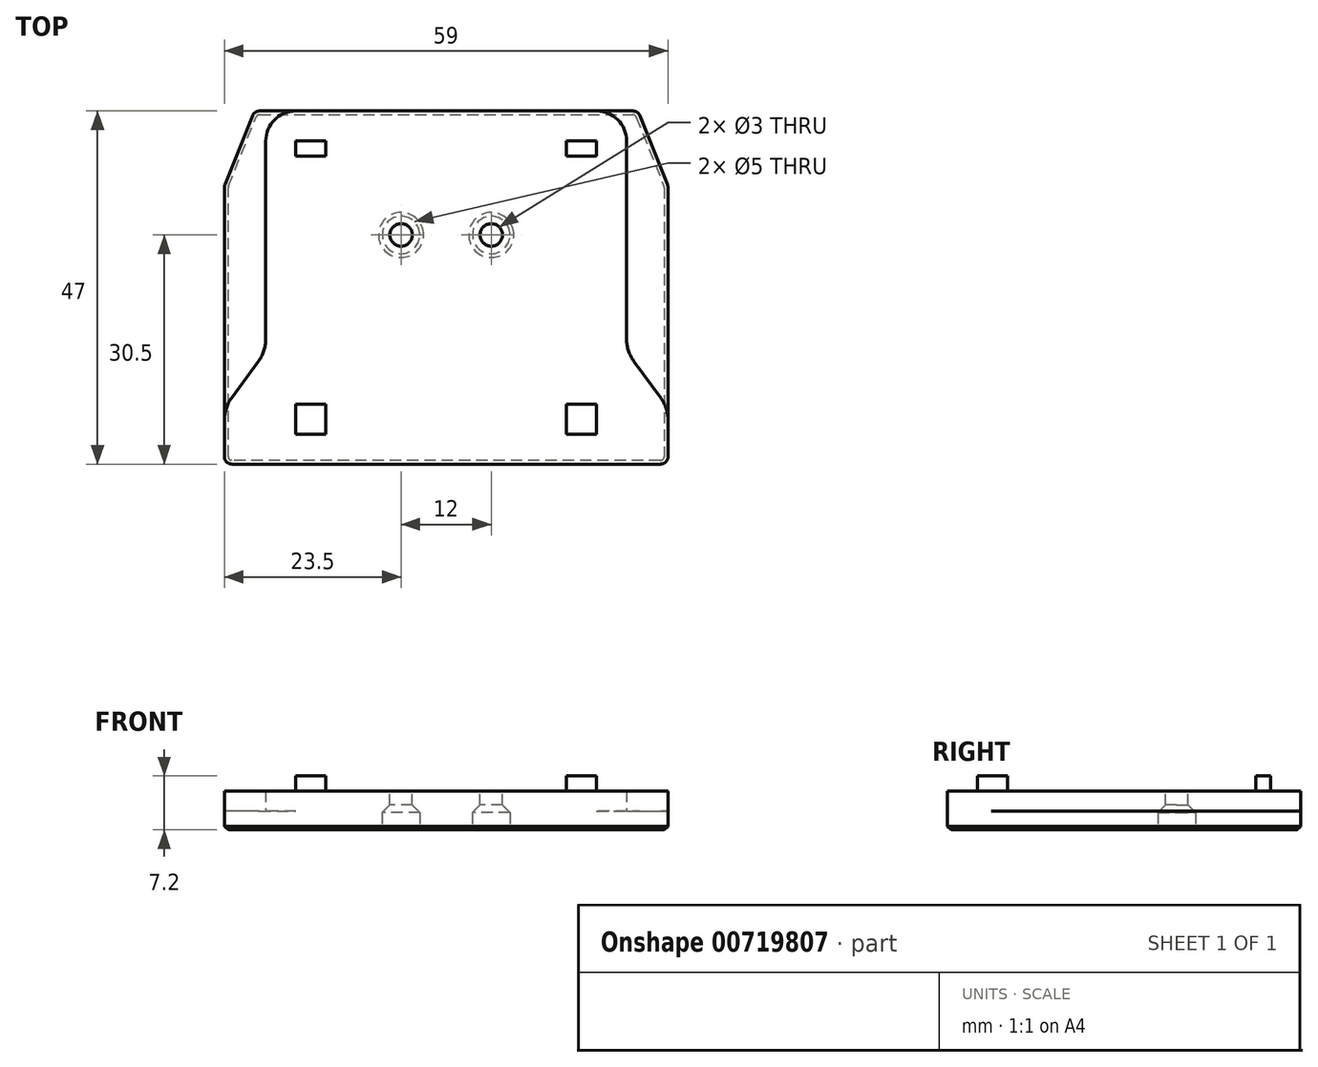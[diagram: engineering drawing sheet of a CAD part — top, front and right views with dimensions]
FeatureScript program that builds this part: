
annotation { "Feature Type Name" : "Feature", "Feature Type Description" : "" }
export const myFeature = defineFeature(function(context is Context, id is Id, definition is map)
    precondition{}
    {
        {
            var Q0;
            Q0=qCreatedBy(makeId("Top.planeOp"),FACE);
            var sketch = newSketch(context, id + "F0", { "sketchPlane" : qUnion([Q0])});
            skLineSegment(sketch, "E0.bottom", {"start": v(4, 0) * mm, "end": v(55, 0) * mm});
            skLineSegment(sketch, "E0.top", {"start": v(0, -47) * mm, "end": v(59, -47) * mm});
            skLineSegment(sketch, "E0.left", {"start": v(0, -10) * mm, "end": v(0, -47) * mm});
            skLineSegment(sketch, "E0.right", {"start": v(59, -10) * mm, "end": v(59, -47) * mm});
            skLineSegment(sketch, "E1", {"start": v(4, 0) * mm, "end": v(0, -10) * mm});
            skPoint(sketch, "E2.orphan", {"position": v(0, 0) * mm});
            skLineSegment(sketch, "E3", {"start": v(55, 0) * mm, "end": v(59, -10) * mm});
            skPoint(sketch, "E4.orphan", {"position": v(59, 0) * mm});
            skSolve(sketch);
        }
        {
            var Q0;
            Q0=makeQuery(id+"F0.imprint","IMPRINT",FACE,{"disambiguationData":[TD([[makeQuery(id+"F0.imprint","IMPRINT",EDGE,{"derivedFrom":sQuery(id+"F0.wireOp",EDGE,"E0.bottom")}),-1.0]])]});
            extrude(context, id + "F1", {"entities" : qUnion([Q0]), "depth" : 2.5 * mm, "offsetDistance" : 25 * mm});
        }
        {
            var Q0;
            Q0=makeQuery(id+"F1.opExtrude","CAP_FACE",FACE,{"disambiguationData":[OSD([sQuery(id+"F0.wireOp",EDGE,"E0.bottom"),sQuery(id+"F0.wireOp",EDGE,"E0.top"),sQuery(id+"F0.wireOp",EDGE,"E0.left"),sQuery(id+"F0.wireOp",EDGE,"E0.right"),sQuery(id+"F0.wireOp",EDGE,"E1"),sQuery(id+"F0.wireOp",EDGE,"E3")])],"isStart":false});
            var sketch = newSketch(context, id + "F2", { "sketchPlane" : qUnion([Q0])});
            skLineSegment(sketch, "E5.bottom", {"start": v(0, -47) * mm, "end": v(59, -47) * mm});
            skLineSegment(sketch, "E5.left", {"start": v(0, -47) * mm, "end": v(0, -39.5) * mm});
            skLineSegment(sketch, "E5.right", {"start": v(59, -47) * mm, "end": v(59, -39.5) * mm});
            skLineSegment(sketch, "E6.top", {"start": v(9.5, 0) * mm, "end": v(49.5, 0) * mm});
            skLineSegment(sketch, "E6.left", {"start": v(5.5, -32) * mm, "end": v(5.5, -4) * mm});
            skLineSegment(sketch, "E6.right", {"start": v(53.5, -32) * mm, "end": v(53.5, -4) * mm});
            skPoint(sketch, "E7.visualSharp", {"position": v(5.5, 0) * mm});
            skArc(sketch, "E7.filletArc", {"start": v(9.5, 0) * mm, "mid": v(6.67, -1.17) * mm, "end": v(5.5, -4) * mm});
            skPoint(sketch, "E8.visualSharp", {"position": v(53.5, 0) * mm});
            skArc(sketch, "E8.filletArc", {"start": v(53.5, -4) * mm, "mid": v(52.33, -1.17) * mm, "end": v(49.5, 0) * mm});
            skLineSegment(sketch, "E9", {"start": v(53.5, -32) * mm, "end": v(59, -39.5) * mm});
            skLineSegment(sketch, "E10", {"start": v(5.5, -32) * mm, "end": v(0, -39.5) * mm});
            skPoint(sketch, "E11.orphan", {"position": v(0, -32) * mm});
            skPoint(sketch, "E12.orphan", {"position": v(59, -32) * mm});
            skSolve(sketch);
        }
        {
            var Q0;
            Q0=makeQuery(id+"F2.imprint","IMPRINT",FACE,{"disambiguationData":[TD([[makeQuery(id+"F2.imprint","IMPRINT",EDGE,{"derivedFrom":sQuery(id+"F2.wireOp",EDGE,"E5.bottom")}),1.0]])]});
            extrude(context, id + "F3", {"entities" : qUnion([Q0]), "operationType" : NewBodyOperationType.ADD, "depth" : 2.7 * mm, "offsetDistance" : 25 * mm});
        }
        {
            var Q0;
            Q0=makeQuery(id+"F3.boolean.opBoolean","MERGE",EDGE,{"derivedFrom":[makeQuery(id+"F1.opExtrude","SWEPT_EDGE",EDGE,{"disambiguationData":[OSD([sQuery(id+"F0.wireOp",EDGE,"E0.top"),sQuery(id+"F0.wireOp",EDGE,"E0.left")])]}),makeQuery(id+"F3.opExtrude","SWEPT_EDGE",EDGE,{"disambiguationData":[OSD([sQuery(id+"F2.wireOp",EDGE,"E5.bottom"),sQuery(id+"F2.wireOp",EDGE,"E5.left")])]})]});
            var Q1;
            Q1=makeQuery(id+"F3.boolean.opBoolean","MERGE",EDGE,{"derivedFrom":[makeQuery(id+"F1.opExtrude","SWEPT_EDGE",EDGE,{"disambiguationData":[OSD([sQuery(id+"F0.wireOp",EDGE,"E0.top"),sQuery(id+"F0.wireOp",EDGE,"E0.right")])]}),makeQuery(id+"F3.opExtrude","SWEPT_EDGE",EDGE,{"disambiguationData":[OSD([sQuery(id+"F2.wireOp",EDGE,"E5.bottom"),sQuery(id+"F2.wireOp",EDGE,"E5.right")])]})]});
            var Q2;
            Q2=makeQuery(id+"F1.opExtrude","SWEPT_EDGE",EDGE,{"disambiguationData":[OSD([sQuery(id+"F0.wireOp",EDGE,"E0.bottom"),sQuery(id+"F0.wireOp",EDGE,"E1")])]});
            var Q3;
            Q3=makeQuery(id+"F1.opExtrude","SWEPT_EDGE",EDGE,{"disambiguationData":[OSD([sQuery(id+"F0.wireOp",EDGE,"E0.bottom"),sQuery(id+"F0.wireOp",EDGE,"E3")])]});
            var Q4;
            Q4=makeQuery(id+"F1.opExtrude","SWEPT_EDGE",EDGE,{"disambiguationData":[OSD([sQuery(id+"F0.wireOp",EDGE,"E0.right"),sQuery(id+"F0.wireOp",EDGE,"E3")])]});
            var Q5;
            Q5=makeQuery(id+"F1.opExtrude","SWEPT_EDGE",EDGE,{"disambiguationData":[OSD([sQuery(id+"F0.wireOp",EDGE,"E0.left"),sQuery(id+"F0.wireOp",EDGE,"E1")])]});
            fillet(context, id + "F4", {"entities" : qUnion([Q0, Q1, Q2, Q3, Q4, Q5]), "radius" : 1 * mm, "tangentPropagation" : true, "allowEdgeOverflow" : false});
        }
        {
            var Q0;
            Q0=makeQuery(id+"F3.opExtrude","SWEPT_EDGE",EDGE,{"disambiguationData":[OSD([sQuery(id+"F0.wireOp",EDGE,"E0.left"),sQuery(id+"F2.wireOp",EDGE,"E5.left"),sQuery(id+"F2.wireOp",EDGE,"E10")])]});
            var Q1;
            Q1=makeQuery(id+"F3.opExtrude","SWEPT_EDGE",EDGE,{"disambiguationData":[OSD([sQuery(id+"F0.wireOp",EDGE,"E0.right"),sQuery(id+"F2.wireOp",EDGE,"E5.right"),sQuery(id+"F2.wireOp",EDGE,"E9")])]});
            var Q2;
            Q2=makeQuery(id+"F3.opExtrude","SWEPT_EDGE",EDGE,{"disambiguationData":[OSD([sQuery(id+"F2.wireOp",EDGE,"E6.right"),sQuery(id+"F2.wireOp",EDGE,"E9")])]});
            var Q3;
            Q3=makeQuery(id+"F3.opExtrude","SWEPT_EDGE",EDGE,{"disambiguationData":[OSD([sQuery(id+"F2.wireOp",EDGE,"E6.left"),sQuery(id+"F2.wireOp",EDGE,"E10")])]});
            fillet(context, id + "F5", {"entities" : qUnion([Q0, Q1, Q2, Q3]), "radius" : 5 * mm, "tangentPropagation" : true, "allowEdgeOverflow" : false});
        }
        {
            var Q0;
            Q0=makeQuery(id+"F3.opExtrude","CAP_FACE",FACE,{"disambiguationData":[OSD([sQuery(id+"F2.wireOp",EDGE,"E5.bottom"),sQuery(id+"F2.wireOp",EDGE,"E5.left"),sQuery(id+"F2.wireOp",EDGE,"E5.right"),sQuery(id+"F2.wireOp",EDGE,"E6.top"),sQuery(id+"F2.wireOp",EDGE,"E6.left"),sQuery(id+"F2.wireOp",EDGE,"E6.right"),sQuery(id+"F2.wireOp",EDGE,"E7.filletArc"),sQuery(id+"F2.wireOp",EDGE,"E8.filletArc"),sQuery(id+"F2.wireOp",EDGE,"E9"),sQuery(id+"F2.wireOp",EDGE,"E10")])],"isStart":false});
            var sketch = newSketch(context, id + "F6", { "sketchPlane" : qUnion([Q0])});
            skLineSegment(sketch, "E13.bottom", {"start": v(9.5, -4) * mm, "end": v(13.5, -4) * mm});
            skLineSegment(sketch, "E13.top", {"start": v(9.5, -6) * mm, "end": v(13.5, -6) * mm});
            skLineSegment(sketch, "E13.left", {"start": v(9.5, -4) * mm, "end": v(9.5, -6) * mm});
            skLineSegment(sketch, "E13.right", {"start": v(13.5, -4) * mm, "end": v(13.5, -6) * mm});
            skLineSegment(sketch, "E14.bottom", {"start": v(9.5, -39) * mm, "end": v(13.5, -39) * mm});
            skLineSegment(sketch, "E14.top", {"start": v(9.5, -43) * mm, "end": v(13.5, -43) * mm});
            skLineSegment(sketch, "E14.left", {"start": v(9.5, -39) * mm, "end": v(9.5, -43) * mm});
            skLineSegment(sketch, "E14.right", {"start": v(13.5, -39) * mm, "end": v(13.5, -43) * mm});
            skLineSegment(sketch, "E15.bottom", {"start": v(45.5, -4) * mm, "end": v(49.5, -4) * mm});
            skLineSegment(sketch, "E15.top", {"start": v(45.5, -6) * mm, "end": v(49.5, -6) * mm});
            skLineSegment(sketch, "E15.left", {"start": v(45.5, -4) * mm, "end": v(45.5, -6) * mm});
            skLineSegment(sketch, "E15.right", {"start": v(49.5, -4) * mm, "end": v(49.5, -6) * mm});
            skLineSegment(sketch, "E16.bottom", {"start": v(45.5, -39) * mm, "end": v(49.5, -39) * mm});
            skLineSegment(sketch, "E16.top", {"start": v(45.5, -43) * mm, "end": v(49.5, -43) * mm});
            skLineSegment(sketch, "E16.left", {"start": v(45.5, -39) * mm, "end": v(45.5, -43) * mm});
            skLineSegment(sketch, "E16.right", {"start": v(49.5, -39) * mm, "end": v(49.5, -43) * mm});
            skSolve(sketch);
        }
        {
            var Q0;
            Q0=qSketchRegion(id+"F6",true);
            extrude(context, id + "F7", {"entities" : qUnion([Q0]), "operationType" : NewBodyOperationType.ADD, "depth" : 2 * mm, "offsetDistance" : 25 * mm});
        }
        {
            var Q0;
            Q0=makeQuery(id+"F6.imprint","IMPRINT",FACE,{"disambiguationData":[TD([[makeQuery(id+"F6.imprint","IMPRINT",EDGE,{"derivedFrom":sQuery(id+"F6.wireOp",EDGE,"E13.bottom")}),1.0]])]});
            var sketch = newSketch(context, id + "F8", { "sketchPlane" : qUnion([Q0])});
            skCircle(sketch, "E17", {"center": v(23.5, -16.5) * mm, "radius": 1.5 * mm});
            skCircle(sketch, "E18", {"center": v(35.5, -16.5) * mm, "radius": 1.5 * mm});
            skSolve(sketch);
        }
        {
            var Q0;
            Q0=qSketchRegion(id+"F8",true);
            extrude(context, id + "F9", {"entities" : qUnion([Q0]), "operationType" : NewBodyOperationType.REMOVE, "oppositeDirection" : true, "depth" : 6 * mm, "offsetDistance" : 25 * mm});
        }
        {
            var Q0;
            Q0=makeQuery(id+"F0.imprint","IMPRINT",FACE,{"disambiguationData":[TD([[makeQuery(id+"F0.imprint","IMPRINT",EDGE,{"derivedFrom":sQuery(id+"F0.wireOp",EDGE,"E0.bottom")}),-1.0]])]});
            var sketch = newSketch(context, id + "F10", { "sketchPlane" : qUnion([Q0])});
            skCircle(sketch, "E19", {"center": v(35.5, -16.5) * mm, "radius": 2.5 * mm});
            skCircle(sketch, "E20", {"center": v(23.5, -16.5) * mm, "radius": 2.5 * mm});
            skSolve(sketch);
        }
        {
            var Q0;
            Q0=qSketchRegion(id+"F10",true);
            extrude(context, id + "F11", {"entities" : qUnion([Q0]), "operationType" : NewBodyOperationType.REMOVE, "depth" : 3.5 * mm, "offsetDistance" : 25 * mm});
        }
        {
            var Q0;
            Q0=makeQuery(id+"F11.boolean.opBoolean","COPY",EDGE,{"derivedFrom":makeQuery(id+"F11.opExtrude","CAP_EDGE",EDGE,{"disambiguationData":[OSD([sQuery(id+"F10.wireOp",EDGE,"E19")])],"isStart":false})});
            var Q1;
            Q1=makeQuery(id+"F11.boolean.opBoolean","COPY",EDGE,{"derivedFrom":makeQuery(id+"F11.opExtrude","CAP_EDGE",EDGE,{"disambiguationData":[OSD([sQuery(id+"F10.wireOp",EDGE,"E20")])],"isStart":false})});
            chamfer(context, id + "F12", {"entities" : qUnion([Q0, Q1]), "width" : 1.2 * mm, "tangentPropagation" : true});
        }
        {
            var Q0;
            Q0=makeQuery(id+"F1.opExtrude","CAP_FACE",FACE,{"disambiguationData":[OSD([sQuery(id+"F0.wireOp",EDGE,"E0.bottom"),sQuery(id+"F0.wireOp",EDGE,"E0.top"),sQuery(id+"F0.wireOp",EDGE,"E0.left"),sQuery(id+"F0.wireOp",EDGE,"E0.right"),sQuery(id+"F0.wireOp",EDGE,"E1"),sQuery(id+"F0.wireOp",EDGE,"E3")])],"isStart":true});
            chamfer(context, id + "F13", {"entities" : qUnion([Q0]), "width" : 0.5 * mm, "tangentPropagation" : true});
        }
    });
